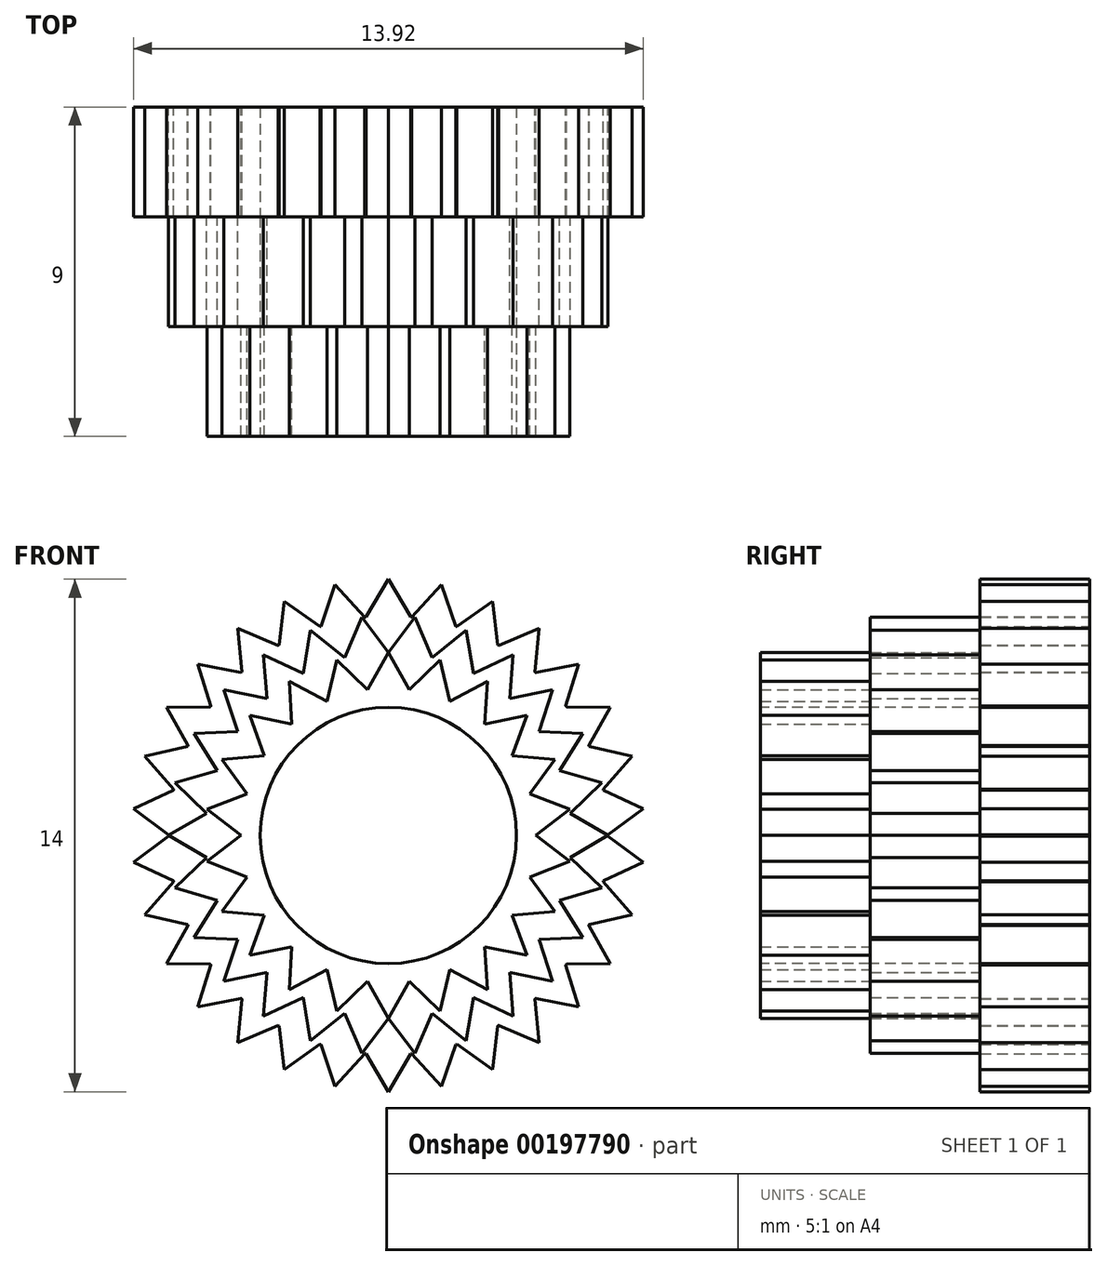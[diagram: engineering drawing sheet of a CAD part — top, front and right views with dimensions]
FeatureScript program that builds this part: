
annotation { "Feature Type Name" : "Feature", "Feature Type Description" : "" }
export const myFeature = defineFeature(function(context is Context, id is Id, definition is map)
    precondition{}
    {
        {
            var Q0;
            Q0=qCreatedBy(makeId("Front.planeOp"),FACE);
            var sketch = newSketch(context, id + "F0", { "sketchPlane" : qUnion([Q0])});
            skCircle(sketch, "E0", {"center": v(0, 0) * mm, "radius": 6 * mm});
            skLineSegment(sketch, "E1", {"start": v(0, 6) * mm, "end": v(0, 7) * mm, "construction": true});
            skLineSegment(sketch, "E2", {"start": v(0, 7) * mm, "end": v(-0.61, 5.97) * mm});
            skLineSegment(sketch, "E3.MirrorCS", {"start": v(0, 7) * mm, "end": v(0.61, 5.97) * mm});
            skLineSegment(sketch, "E4.1.0", {"start": v(-1.46, 6.85) * mm, "end": v(-0.64, 5.97) * mm});
            skLineSegment(sketch, "E4.1.1", {"start": v(-1.46, 6.85) * mm, "end": v(-1.84, 5.71) * mm});
            skLineSegment(sketch, "E4.2.0", {"start": v(-2.85, 6.4) * mm, "end": v(-1.87, 5.7) * mm});
            skLineSegment(sketch, "E4.2.1", {"start": v(-2.85, 6.4) * mm, "end": v(-2.99, 5.2) * mm});
            skLineSegment(sketch, "E4.3.0", {"start": v(-4.11, 5.66) * mm, "end": v(-3.01, 5.19) * mm});
            skLineSegment(sketch, "E4.3.1", {"start": v(-4.11, 5.66) * mm, "end": v(-4, 4.47) * mm});
            skLineSegment(sketch, "E4.4.0", {"start": v(-5.2, 4.68) * mm, "end": v(-4.03, 4.45) * mm});
            skLineSegment(sketch, "E4.4.1", {"start": v(-5.2, 4.68) * mm, "end": v(-4.85, 3.54) * mm});
            skLineSegment(sketch, "E4.5.0", {"start": v(-6.06, 3.5) * mm, "end": v(-4.86, 3.52) * mm});
            skLineSegment(sketch, "E4.5.1", {"start": v(-6.06, 3.5) * mm, "end": v(-5.48, 2.45) * mm});
            skLineSegment(sketch, "E4.6.0", {"start": v(-6.66, 2.16) * mm, "end": v(-5.49, 2.43) * mm});
            skLineSegment(sketch, "E4.6.1", {"start": v(-6.66, 2.16) * mm, "end": v(-5.87, 1.26) * mm});
            skLineSegment(sketch, "E4.7.0", {"start": v(-6.96, 0.73) * mm, "end": v(-5.87, 1.23) * mm});
            skLineSegment(sketch, "E4.7.1", {"start": v(-6.96, 0.73) * mm, "end": v(-6, 0.01) * mm});
            skLineSegment(sketch, "E4.8.0", {"start": v(-6.96, -0.73) * mm, "end": v(-6, -0.01) * mm});
            skLineSegment(sketch, "E4.8.1", {"start": v(-6.96, -0.73) * mm, "end": v(-5.87, -1.23) * mm});
            skLineSegment(sketch, "E4.9.0", {"start": v(-6.66, -2.16) * mm, "end": v(-5.87, -1.26) * mm});
            skLineSegment(sketch, "E4.9.1", {"start": v(-6.66, -2.16) * mm, "end": v(-5.49, -2.43) * mm});
            skLineSegment(sketch, "E4.10.0", {"start": v(-6.06, -3.5) * mm, "end": v(-5.48, -2.45) * mm});
            skLineSegment(sketch, "E4.10.1", {"start": v(-6.06, -3.5) * mm, "end": v(-4.86, -3.52) * mm});
            skLineSegment(sketch, "E4.11.0", {"start": v(-5.2, -4.68) * mm, "end": v(-4.85, -3.54) * mm});
            skLineSegment(sketch, "E4.11.1", {"start": v(-5.2, -4.68) * mm, "end": v(-4.03, -4.45) * mm});
            skLineSegment(sketch, "E4.12.0", {"start": v(-4.11, -5.66) * mm, "end": v(-4, -4.47) * mm});
            skLineSegment(sketch, "E4.12.1", {"start": v(-4.11, -5.66) * mm, "end": v(-3.01, -5.19) * mm});
            skLineSegment(sketch, "E4.13.0", {"start": v(-2.85, -6.4) * mm, "end": v(-2.99, -5.2) * mm});
            skLineSegment(sketch, "E4.13.1", {"start": v(-2.85, -6.4) * mm, "end": v(-1.87, -5.7) * mm});
            skLineSegment(sketch, "E4.14.0", {"start": v(-1.46, -6.85) * mm, "end": v(-1.84, -5.71) * mm});
            skLineSegment(sketch, "E4.14.1", {"start": v(-1.46, -6.85) * mm, "end": v(-0.64, -5.97) * mm});
            skLineSegment(sketch, "E4.15.0", {"start": v(0, -7) * mm, "end": v(-0.61, -5.97) * mm});
            skLineSegment(sketch, "E4.15.1", {"start": v(0, -7) * mm, "end": v(0.61, -5.97) * mm});
            skLineSegment(sketch, "E4.16.0", {"start": v(1.46, -6.85) * mm, "end": v(0.64, -5.97) * mm});
            skLineSegment(sketch, "E4.16.1", {"start": v(1.46, -6.85) * mm, "end": v(1.84, -5.71) * mm});
            skLineSegment(sketch, "E4.17.0", {"start": v(2.85, -6.4) * mm, "end": v(1.87, -5.7) * mm});
            skLineSegment(sketch, "E4.17.1", {"start": v(2.85, -6.4) * mm, "end": v(2.99, -5.2) * mm});
            skLineSegment(sketch, "E4.18.0", {"start": v(4.11, -5.66) * mm, "end": v(3.01, -5.19) * mm});
            skLineSegment(sketch, "E4.18.1", {"start": v(4.11, -5.66) * mm, "end": v(4, -4.47) * mm});
            skLineSegment(sketch, "E4.19.0", {"start": v(5.2, -4.68) * mm, "end": v(4.03, -4.45) * mm});
            skLineSegment(sketch, "E4.19.1", {"start": v(5.2, -4.68) * mm, "end": v(4.85, -3.54) * mm});
            skLineSegment(sketch, "E4.20.0", {"start": v(6.06, -3.5) * mm, "end": v(4.86, -3.52) * mm});
            skLineSegment(sketch, "E4.20.1", {"start": v(6.06, -3.5) * mm, "end": v(5.48, -2.45) * mm});
            skLineSegment(sketch, "E4.21.0", {"start": v(6.66, -2.16) * mm, "end": v(5.49, -2.43) * mm});
            skLineSegment(sketch, "E4.21.1", {"start": v(6.66, -2.16) * mm, "end": v(5.87, -1.26) * mm});
            skLineSegment(sketch, "E4.22.0", {"start": v(6.96, -0.73) * mm, "end": v(5.87, -1.23) * mm});
            skLineSegment(sketch, "E4.22.1", {"start": v(6.96, -0.73) * mm, "end": v(6, -0.01) * mm});
            skLineSegment(sketch, "E4.23.0", {"start": v(6.96, 0.73) * mm, "end": v(6, 0.01) * mm});
            skLineSegment(sketch, "E4.23.1", {"start": v(6.96, 0.73) * mm, "end": v(5.87, 1.23) * mm});
            skLineSegment(sketch, "E4.24.0", {"start": v(6.66, 2.16) * mm, "end": v(5.87, 1.26) * mm});
            skLineSegment(sketch, "E4.24.1", {"start": v(6.66, 2.16) * mm, "end": v(5.49, 2.43) * mm});
            skLineSegment(sketch, "E4.25.0", {"start": v(6.06, 3.5) * mm, "end": v(5.48, 2.45) * mm});
            skLineSegment(sketch, "E4.25.1", {"start": v(6.06, 3.5) * mm, "end": v(4.86, 3.52) * mm});
            skLineSegment(sketch, "E4.26.0", {"start": v(5.2, 4.68) * mm, "end": v(4.85, 3.54) * mm});
            skLineSegment(sketch, "E4.26.1", {"start": v(5.2, 4.68) * mm, "end": v(4.03, 4.45) * mm});
            skLineSegment(sketch, "E4.27.0", {"start": v(4.11, 5.66) * mm, "end": v(4, 4.47) * mm});
            skLineSegment(sketch, "E4.27.1", {"start": v(4.11, 5.66) * mm, "end": v(3.01, 5.19) * mm});
            skLineSegment(sketch, "E4.28.0", {"start": v(2.85, 6.4) * mm, "end": v(2.99, 5.2) * mm});
            skLineSegment(sketch, "E4.28.1", {"start": v(2.85, 6.4) * mm, "end": v(1.87, 5.7) * mm});
            skLineSegment(sketch, "E4.29.0", {"start": v(1.46, 6.85) * mm, "end": v(1.84, 5.71) * mm});
            skLineSegment(sketch, "E4.29.1", {"start": v(1.46, 6.85) * mm, "end": v(0.64, 5.97) * mm});
            skSolve(sketch);
        }
        {
            var Q0;
            Q0 = qSketchRegion(id + "F0", true);
            extrude(context, id + "F1", {"entities" : qUnion([Q0]), "depth" : 3 * mm});
        }
        {
            var Q0;
            Q0=makeQuery(id+"F1.opExtrude","CAP_FACE",FACE,{"disambiguationData":[OSD([sQuery(id+"F0.wireOp",EDGE,"E0"),sQuery(id+"F0.wireOp",EDGE,"E2"),sQuery(id+"F0.wireOp",EDGE,"E3.MirrorCS"),sQuery(id+"F0.wireOp",EDGE,"E4.1.0"),sQuery(id+"F0.wireOp",EDGE,"E4.1.1"),sQuery(id+"F0.wireOp",EDGE,"E4.2.0"),sQuery(id+"F0.wireOp",EDGE,"E4.2.1"),sQuery(id+"F0.wireOp",EDGE,"E4.3.0"),sQuery(id+"F0.wireOp",EDGE,"E4.3.1"),sQuery(id+"F0.wireOp",EDGE,"E4.4.0"),sQuery(id+"F0.wireOp",EDGE,"E4.4.1"),sQuery(id+"F0.wireOp",EDGE,"E4.5.0"),sQuery(id+"F0.wireOp",EDGE,"E4.5.1"),sQuery(id+"F0.wireOp",EDGE,"E4.6.0"),sQuery(id+"F0.wireOp",EDGE,"E4.6.1"),sQuery(id+"F0.wireOp",EDGE,"E4.7.0"),sQuery(id+"F0.wireOp",EDGE,"E4.7.1"),sQuery(id+"F0.wireOp",EDGE,"E4.8.0"),sQuery(id+"F0.wireOp",EDGE,"E4.8.1"),sQuery(id+"F0.wireOp",EDGE,"E4.9.0"),sQuery(id+"F0.wireOp",EDGE,"E4.9.1"),sQuery(id+"F0.wireOp",EDGE,"E4.10.0"),sQuery(id+"F0.wireOp",EDGE,"E4.10.1"),sQuery(id+"F0.wireOp",EDGE,"E4.11.0"),sQuery(id+"F0.wireOp",EDGE,"E4.11.1"),sQuery(id+"F0.wireOp",EDGE,"E4.12.0"),sQuery(id+"F0.wireOp",EDGE,"E4.12.1"),sQuery(id+"F0.wireOp",EDGE,"E4.13.0"),sQuery(id+"F0.wireOp",EDGE,"E4.13.1"),sQuery(id+"F0.wireOp",EDGE,"E4.14.0"),sQuery(id+"F0.wireOp",EDGE,"E4.14.1"),sQuery(id+"F0.wireOp",EDGE,"E4.15.0"),sQuery(id+"F0.wireOp",EDGE,"E4.15.1"),sQuery(id+"F0.wireOp",EDGE,"E4.16.0"),sQuery(id+"F0.wireOp",EDGE,"E4.16.1"),sQuery(id+"F0.wireOp",EDGE,"E4.17.0"),sQuery(id+"F0.wireOp",EDGE,"E4.17.1"),sQuery(id+"F0.wireOp",EDGE,"E4.18.0"),sQuery(id+"F0.wireOp",EDGE,"E4.18.1"),sQuery(id+"F0.wireOp",EDGE,"E4.19.0"),sQuery(id+"F0.wireOp",EDGE,"E4.19.1"),sQuery(id+"F0.wireOp",EDGE,"E4.20.0"),sQuery(id+"F0.wireOp",EDGE,"E4.20.1"),sQuery(id+"F0.wireOp",EDGE,"E4.21.0"),sQuery(id+"F0.wireOp",EDGE,"E4.21.1"),sQuery(id+"F0.wireOp",EDGE,"E4.22.0"),sQuery(id+"F0.wireOp",EDGE,"E4.22.1"),sQuery(id+"F0.wireOp",EDGE,"E4.23.0"),sQuery(id+"F0.wireOp",EDGE,"E4.23.1"),sQuery(id+"F0.wireOp",EDGE,"E4.24.0"),sQuery(id+"F0.wireOp",EDGE,"E4.24.1"),sQuery(id+"F0.wireOp",EDGE,"E4.25.0"),sQuery(id+"F0.wireOp",EDGE,"E4.25.1"),sQuery(id+"F0.wireOp",EDGE,"E4.26.0"),sQuery(id+"F0.wireOp",EDGE,"E4.26.1"),sQuery(id+"F0.wireOp",EDGE,"E4.27.0"),sQuery(id+"F0.wireOp",EDGE,"E4.27.1"),sQuery(id+"F0.wireOp",EDGE,"E4.28.0"),sQuery(id+"F0.wireOp",EDGE,"E4.28.1"),sQuery(id+"F0.wireOp",EDGE,"E4.29.0"),sQuery(id+"F0.wireOp",EDGE,"E4.29.1")])],"isStart":false});
            var sketch = newSketch(context, id + "F2", { "sketchPlane" : qUnion([Q0])});
            skCircle(sketch, "E5", {"center": v(0, 0) * mm, "radius": 5 * mm});
            skLineSegment(sketch, "E6", {"start": v(5, 0) * mm, "end": v(6, 0) * mm, "construction": true});
            skLineSegment(sketch, "E7", {"start": v(6, 0) * mm, "end": v(4.96, 0.6) * mm});
            skLineSegment(sketch, "E8.MirrorCS", {"start": v(6, 0) * mm, "end": v(4.96, -0.6) * mm});
            skLineSegment(sketch, "E9.1.0", {"start": v(5.83, 1.44) * mm, "end": v(4.67, 1.77) * mm});
            skLineSegment(sketch, "E9.1.1", {"start": v(5.83, 1.44) * mm, "end": v(4.96, 0.6) * mm});
            skLineSegment(sketch, "E9.2.0", {"start": v(5.31, 2.79) * mm, "end": v(4.11, 2.84) * mm});
            skLineSegment(sketch, "E9.2.1", {"start": v(5.31, 2.79) * mm, "end": v(4.68, 1.77) * mm});
            skLineSegment(sketch, "E9.3.0", {"start": v(4.5, 3.98) * mm, "end": v(3.31, 3.74) * mm});
            skLineSegment(sketch, "E9.3.1", {"start": v(4.5, 3.98) * mm, "end": v(4.12, 2.84) * mm});
            skLineSegment(sketch, "E9.4.0", {"start": v(3.4, 4.94) * mm, "end": v(2.32, 4.43) * mm});
            skLineSegment(sketch, "E9.4.1", {"start": v(3.4, 4.94) * mm, "end": v(3.32, 3.74) * mm});
            skLineSegment(sketch, "E9.5.0", {"start": v(2.13, 5.61) * mm, "end": v(1.2, 4.86) * mm});
            skLineSegment(sketch, "E9.5.1", {"start": v(2.13, 5.61) * mm, "end": v(2.33, 4.43) * mm});
            skLineSegment(sketch, "E9.6.0", {"start": v(0.72, 5.96) * mm, "end": v(0, 5) * mm});
            skLineSegment(sketch, "E9.6.1", {"start": v(0.72, 5.96) * mm, "end": v(1.2, 4.85) * mm});
            skLineSegment(sketch, "E9.7.0", {"start": v(-0.72, 5.96) * mm, "end": v(-1.2, 4.85) * mm});
            skLineSegment(sketch, "E9.7.1", {"start": v(-0.72, 5.96) * mm, "end": v(0, 5) * mm});
            skLineSegment(sketch, "E9.8.0", {"start": v(-2.13, 5.61) * mm, "end": v(-2.33, 4.43) * mm});
            skLineSegment(sketch, "E9.8.1", {"start": v(-2.13, 5.61) * mm, "end": v(-1.2, 4.86) * mm});
            skLineSegment(sketch, "E9.9.0", {"start": v(-3.4, 4.94) * mm, "end": v(-3.32, 3.74) * mm});
            skLineSegment(sketch, "E9.9.1", {"start": v(-3.4, 4.94) * mm, "end": v(-2.32, 4.43) * mm});
            skLineSegment(sketch, "E9.10.0", {"start": v(-4.5, 3.98) * mm, "end": v(-4.12, 2.84) * mm});
            skLineSegment(sketch, "E9.10.1", {"start": v(-4.5, 3.98) * mm, "end": v(-3.31, 3.74) * mm});
            skLineSegment(sketch, "E9.11.0", {"start": v(-5.31, 2.79) * mm, "end": v(-4.68, 1.77) * mm});
            skLineSegment(sketch, "E9.11.1", {"start": v(-5.31, 2.79) * mm, "end": v(-4.11, 2.84) * mm});
            skLineSegment(sketch, "E9.12.0", {"start": v(-5.83, 1.44) * mm, "end": v(-4.96, 0.6) * mm});
            skLineSegment(sketch, "E9.12.1", {"start": v(-5.83, 1.44) * mm, "end": v(-4.67, 1.77) * mm});
            skLineSegment(sketch, "E9.13.0", {"start": v(-6, 0) * mm, "end": v(-4.96, -0.6) * mm});
            skLineSegment(sketch, "E9.13.1", {"start": v(-6, 0) * mm, "end": v(-4.96, 0.6) * mm});
            skLineSegment(sketch, "E9.14.0", {"start": v(-5.83, -1.44) * mm, "end": v(-4.67, -1.77) * mm});
            skLineSegment(sketch, "E9.14.1", {"start": v(-5.83, -1.44) * mm, "end": v(-4.96, -0.6) * mm});
            skLineSegment(sketch, "E9.15.0", {"start": v(-5.31, -2.79) * mm, "end": v(-4.11, -2.84) * mm});
            skLineSegment(sketch, "E9.15.1", {"start": v(-5.31, -2.79) * mm, "end": v(-4.68, -1.77) * mm});
            skLineSegment(sketch, "E9.16.0", {"start": v(-4.5, -3.98) * mm, "end": v(-3.31, -3.74) * mm});
            skLineSegment(sketch, "E9.16.1", {"start": v(-4.5, -3.98) * mm, "end": v(-4.12, -2.84) * mm});
            skLineSegment(sketch, "E9.17.0", {"start": v(-3.4, -4.94) * mm, "end": v(-2.32, -4.43) * mm});
            skLineSegment(sketch, "E9.17.1", {"start": v(-3.4, -4.94) * mm, "end": v(-3.32, -3.74) * mm});
            skLineSegment(sketch, "E9.18.0", {"start": v(-2.13, -5.61) * mm, "end": v(-1.2, -4.86) * mm});
            skLineSegment(sketch, "E9.18.1", {"start": v(-2.13, -5.61) * mm, "end": v(-2.33, -4.43) * mm});
            skLineSegment(sketch, "E9.19.0", {"start": v(-0.72, -5.96) * mm, "end": v(0, -5) * mm});
            skLineSegment(sketch, "E9.19.1", {"start": v(-0.72, -5.96) * mm, "end": v(-1.2, -4.85) * mm});
            skLineSegment(sketch, "E9.20.0", {"start": v(0.72, -5.96) * mm, "end": v(1.2, -4.85) * mm});
            skLineSegment(sketch, "E9.20.1", {"start": v(0.72, -5.96) * mm, "end": v(0, -5) * mm});
            skLineSegment(sketch, "E9.21.0", {"start": v(2.13, -5.61) * mm, "end": v(2.33, -4.43) * mm});
            skLineSegment(sketch, "E9.21.1", {"start": v(2.13, -5.61) * mm, "end": v(1.2, -4.86) * mm});
            skLineSegment(sketch, "E9.22.0", {"start": v(3.4, -4.94) * mm, "end": v(3.32, -3.74) * mm});
            skLineSegment(sketch, "E9.22.1", {"start": v(3.4, -4.94) * mm, "end": v(2.32, -4.43) * mm});
            skLineSegment(sketch, "E9.23.0", {"start": v(4.5, -3.98) * mm, "end": v(4.12, -2.84) * mm});
            skLineSegment(sketch, "E9.23.1", {"start": v(4.5, -3.98) * mm, "end": v(3.31, -3.74) * mm});
            skLineSegment(sketch, "E9.24.0", {"start": v(5.31, -2.79) * mm, "end": v(4.68, -1.77) * mm});
            skLineSegment(sketch, "E9.24.1", {"start": v(5.31, -2.79) * mm, "end": v(4.11, -2.84) * mm});
            skLineSegment(sketch, "E9.25.0", {"start": v(5.83, -1.44) * mm, "end": v(4.96, -0.6) * mm});
            skLineSegment(sketch, "E9.25.1", {"start": v(5.83, -1.44) * mm, "end": v(4.67, -1.77) * mm});
            skSolve(sketch);
        }
        {
            var Q0;
            Q0 = qSketchRegion(id + "F2", true);
            var Q1;
            {var subQ0=sQuery(id+"F2.wireOp",EDGE,"E5");var subQ42=makeQuery(id+"F2.imprint","INTERSECT",VERTEX,{"derivedFrom":[subQ0,sQuery(id+"F2.wireOp",EDGE,"E7")]});Q1=makeQuery(id+"F2.imprint","IMPRINT",FACE,{"disambiguationData":[TD([[makeQuery(id+"F2.imprint","IMPRINT",EDGE,{"disambiguationData":[TD([[subQ42,1.0]])],"derivedFrom":subQ0}),1.0]])]});}
            extrude(context, id + "F3", {"entities" : qUnion([Q0, Q1]), "depth" : 3 * mm});
        }
        {
            var Q0;
            Q0=makeQuery(id+"F3.opExtrude","CAP_FACE",FACE,{"disambiguationData":[OSD([sQuery(id+"F2.wireOp",EDGE,"E7"),sQuery(id+"F2.wireOp",EDGE,"E8.MirrorCS"),sQuery(id+"F2.wireOp",EDGE,"E9.1.0"),sQuery(id+"F2.wireOp",EDGE,"E9.1.1"),sQuery(id+"F2.wireOp",EDGE,"E9.2.0"),sQuery(id+"F2.wireOp",EDGE,"E9.2.1"),sQuery(id+"F2.wireOp",EDGE,"E9.3.0"),sQuery(id+"F2.wireOp",EDGE,"E9.3.1"),sQuery(id+"F2.wireOp",EDGE,"E9.4.0"),sQuery(id+"F2.wireOp",EDGE,"E9.4.1"),sQuery(id+"F2.wireOp",EDGE,"E9.5.0"),sQuery(id+"F2.wireOp",EDGE,"E9.5.1"),sQuery(id+"F2.wireOp",EDGE,"E9.6.0"),sQuery(id+"F2.wireOp",EDGE,"E9.6.1"),sQuery(id+"F2.wireOp",EDGE,"E9.7.0"),sQuery(id+"F2.wireOp",EDGE,"E9.7.1"),sQuery(id+"F2.wireOp",EDGE,"E9.8.0"),sQuery(id+"F2.wireOp",EDGE,"E9.8.1"),sQuery(id+"F2.wireOp",EDGE,"E9.9.0"),sQuery(id+"F2.wireOp",EDGE,"E9.9.1"),sQuery(id+"F2.wireOp",EDGE,"E9.10.0"),sQuery(id+"F2.wireOp",EDGE,"E9.10.1"),sQuery(id+"F2.wireOp",EDGE,"E9.11.0"),sQuery(id+"F2.wireOp",EDGE,"E9.11.1"),sQuery(id+"F2.wireOp",EDGE,"E9.12.0"),sQuery(id+"F2.wireOp",EDGE,"E9.12.1"),sQuery(id+"F2.wireOp",EDGE,"E9.13.0"),sQuery(id+"F2.wireOp",EDGE,"E9.13.1"),sQuery(id+"F2.wireOp",EDGE,"E9.14.0"),sQuery(id+"F2.wireOp",EDGE,"E9.14.1"),sQuery(id+"F2.wireOp",EDGE,"E9.15.0"),sQuery(id+"F2.wireOp",EDGE,"E9.15.1"),sQuery(id+"F2.wireOp",EDGE,"E9.16.0"),sQuery(id+"F2.wireOp",EDGE,"E9.16.1"),sQuery(id+"F2.wireOp",EDGE,"E9.17.0"),sQuery(id+"F2.wireOp",EDGE,"E9.17.1"),sQuery(id+"F2.wireOp",EDGE,"E9.18.0"),sQuery(id+"F2.wireOp",EDGE,"E9.18.1"),sQuery(id+"F2.wireOp",EDGE,"E9.19.0"),sQuery(id+"F2.wireOp",EDGE,"E9.19.1"),sQuery(id+"F2.wireOp",EDGE,"E9.20.0"),sQuery(id+"F2.wireOp",EDGE,"E9.20.1"),sQuery(id+"F2.wireOp",EDGE,"E9.21.0"),sQuery(id+"F2.wireOp",EDGE,"E9.21.1"),sQuery(id+"F2.wireOp",EDGE,"E9.22.0"),sQuery(id+"F2.wireOp",EDGE,"E9.22.1"),sQuery(id+"F2.wireOp",EDGE,"E9.23.0"),sQuery(id+"F2.wireOp",EDGE,"E9.23.1"),sQuery(id+"F2.wireOp",EDGE,"E9.24.0"),sQuery(id+"F2.wireOp",EDGE,"E9.24.1"),sQuery(id+"F2.wireOp",EDGE,"E9.25.0"),sQuery(id+"F2.wireOp",EDGE,"E9.25.1")])],"isStart":false});
            var sketch = newSketch(context, id + "F4", { "sketchPlane" : qUnion([Q0])});
            skCircle(sketch, "E10", {"center": v(0, 0) * mm, "radius": 4 * mm});
            skLineSegment(sketch, "E11", {"start": v(0, 4) * mm, "end": v(0, 5) * mm, "construction": true});
            skLineSegment(sketch, "E12", {"start": v(0, 5) * mm, "end": v(-0.59, 3.96) * mm});
            skLineSegment(sketch, "E13.MirrorCS", {"start": v(0, 5) * mm, "end": v(0.59, 3.96) * mm});
            skLineSegment(sketch, "E14.1.0", {"start": v(-1.4, 4.8) * mm, "end": v(-1.68, 3.63) * mm});
            skLineSegment(sketch, "E14.1.1", {"start": v(-1.4, 4.8) * mm, "end": v(-0.55, 3.96) * mm});
            skLineSegment(sketch, "E14.2.0", {"start": v(-2.7, 4.2) * mm, "end": v(-2.63, 3.01) * mm});
            skLineSegment(sketch, "E14.2.1", {"start": v(-2.7, 4.2) * mm, "end": v(-1.64, 3.65) * mm});
            skLineSegment(sketch, "E14.3.0", {"start": v(-3.78, 3.28) * mm, "end": v(-3.38, 2.15) * mm});
            skLineSegment(sketch, "E14.3.1", {"start": v(-3.78, 3.28) * mm, "end": v(-2.6, 3.04) * mm});
            skLineSegment(sketch, "E14.4.0", {"start": v(-4.55, 2.08) * mm, "end": v(-3.84, 1.1) * mm});
            skLineSegment(sketch, "E14.4.1", {"start": v(-4.55, 2.08) * mm, "end": v(-3.35, 2.18) * mm});
            skLineSegment(sketch, "E14.5.0", {"start": v(-4.95, 0.71) * mm, "end": v(-4, -0.02) * mm});
            skLineSegment(sketch, "E14.5.1", {"start": v(-4.95, 0.71) * mm, "end": v(-3.83, 1.15) * mm});
            skLineSegment(sketch, "E14.6.0", {"start": v(-4.95, -0.71) * mm, "end": v(-3.83, -1.15) * mm});
            skLineSegment(sketch, "E14.6.1", {"start": v(-4.95, -0.71) * mm, "end": v(-4, 0.02) * mm});
            skLineSegment(sketch, "E14.7.0", {"start": v(-4.55, -2.08) * mm, "end": v(-3.35, -2.18) * mm});
            skLineSegment(sketch, "E14.7.1", {"start": v(-4.55, -2.08) * mm, "end": v(-3.84, -1.1) * mm});
            skLineSegment(sketch, "E14.8.0", {"start": v(-3.78, -3.28) * mm, "end": v(-2.6, -3.04) * mm});
            skLineSegment(sketch, "E14.8.1", {"start": v(-3.78, -3.28) * mm, "end": v(-3.38, -2.15) * mm});
            skLineSegment(sketch, "E14.9.0", {"start": v(-2.7, -4.2) * mm, "end": v(-1.64, -3.65) * mm});
            skLineSegment(sketch, "E14.9.1", {"start": v(-2.7, -4.2) * mm, "end": v(-2.63, -3.01) * mm});
            skLineSegment(sketch, "E14.10.0", {"start": v(-1.4, -4.8) * mm, "end": v(-0.55, -3.96) * mm});
            skLineSegment(sketch, "E14.10.1", {"start": v(-1.4, -4.8) * mm, "end": v(-1.68, -3.63) * mm});
            skLineSegment(sketch, "E14.11.0", {"start": v(0, -5) * mm, "end": v(0.59, -3.96) * mm});
            skLineSegment(sketch, "E14.11.1", {"start": v(0, -5) * mm, "end": v(-0.59, -3.96) * mm});
            skLineSegment(sketch, "E14.12.0", {"start": v(1.4, -4.8) * mm, "end": v(1.68, -3.63) * mm});
            skLineSegment(sketch, "E14.12.1", {"start": v(1.4, -4.8) * mm, "end": v(0.55, -3.96) * mm});
            skLineSegment(sketch, "E14.13.0", {"start": v(2.7, -4.2) * mm, "end": v(2.63, -3.01) * mm});
            skLineSegment(sketch, "E14.13.1", {"start": v(2.7, -4.2) * mm, "end": v(1.64, -3.65) * mm});
            skLineSegment(sketch, "E14.14.0", {"start": v(3.78, -3.28) * mm, "end": v(3.38, -2.15) * mm});
            skLineSegment(sketch, "E14.14.1", {"start": v(3.78, -3.28) * mm, "end": v(2.6, -3.04) * mm});
            skLineSegment(sketch, "E14.15.0", {"start": v(4.55, -2.08) * mm, "end": v(3.84, -1.1) * mm});
            skLineSegment(sketch, "E14.15.1", {"start": v(4.55, -2.08) * mm, "end": v(3.35, -2.18) * mm});
            skLineSegment(sketch, "E14.16.0", {"start": v(4.95, -0.71) * mm, "end": v(4, 0.02) * mm});
            skLineSegment(sketch, "E14.16.1", {"start": v(4.95, -0.71) * mm, "end": v(3.83, -1.15) * mm});
            skLineSegment(sketch, "E14.17.0", {"start": v(4.95, 0.71) * mm, "end": v(3.83, 1.15) * mm});
            skLineSegment(sketch, "E14.17.1", {"start": v(4.95, 0.71) * mm, "end": v(4, -0.02) * mm});
            skLineSegment(sketch, "E14.18.0", {"start": v(4.55, 2.08) * mm, "end": v(3.35, 2.18) * mm});
            skLineSegment(sketch, "E14.18.1", {"start": v(4.55, 2.08) * mm, "end": v(3.84, 1.1) * mm});
            skLineSegment(sketch, "E14.19.0", {"start": v(3.78, 3.28) * mm, "end": v(2.6, 3.04) * mm});
            skLineSegment(sketch, "E14.19.1", {"start": v(3.78, 3.28) * mm, "end": v(3.38, 2.15) * mm});
            skLineSegment(sketch, "E14.20.0", {"start": v(2.7, 4.2) * mm, "end": v(1.64, 3.65) * mm});
            skLineSegment(sketch, "E14.20.1", {"start": v(2.7, 4.2) * mm, "end": v(2.63, 3.01) * mm});
            skLineSegment(sketch, "E14.21.0", {"start": v(1.4, 4.8) * mm, "end": v(0.55, 3.96) * mm});
            skLineSegment(sketch, "E14.21.1", {"start": v(1.4, 4.8) * mm, "end": v(1.68, 3.63) * mm});
            skSolve(sketch);
        }
        {
            var Q0;
            Q0 = qSketchRegion(id + "F4", true);
            var Q1;
            {var subQ0=sQuery(id+"F4.wireOp",EDGE,"E10");var subQ27=makeQuery(id+"F4.imprint","INTERSECT",VERTEX,{"derivedFrom":[subQ0,sQuery(id+"F4.wireOp",EDGE,"E14.16.0")]});Q1=makeQuery(id+"F4.imprint","IMPRINT",FACE,{"disambiguationData":[TD([[makeQuery(id+"F4.imprint","IMPRINT",EDGE,{"disambiguationData":[TD([[subQ27,-1.0]])],"derivedFrom":subQ0}),1.0]])]});}
            extrude(context, id + "F5", {"entities" : qUnion([Q0, Q1]), "depth" : 3 * mm});
        }
        {
            var Q0;
            Q0=makeQuery(id+"F5.opExtrude","CAP_FACE",FACE,{"disambiguationData":[OSD([sQuery(id+"F4.wireOp",EDGE,"E12"),sQuery(id+"F4.wireOp",EDGE,"E13.MirrorCS"),sQuery(id+"F4.wireOp",EDGE,"E14.1.0"),sQuery(id+"F4.wireOp",EDGE,"E14.1.1"),sQuery(id+"F4.wireOp",EDGE,"E14.2.0"),sQuery(id+"F4.wireOp",EDGE,"E14.2.1"),sQuery(id+"F4.wireOp",EDGE,"E14.3.0"),sQuery(id+"F4.wireOp",EDGE,"E14.3.1"),sQuery(id+"F4.wireOp",EDGE,"E14.4.0"),sQuery(id+"F4.wireOp",EDGE,"E14.4.1"),sQuery(id+"F4.wireOp",EDGE,"E14.5.0"),sQuery(id+"F4.wireOp",EDGE,"E14.5.1"),sQuery(id+"F4.wireOp",EDGE,"E14.6.0"),sQuery(id+"F4.wireOp",EDGE,"E14.6.1"),sQuery(id+"F4.wireOp",EDGE,"E14.7.0"),sQuery(id+"F4.wireOp",EDGE,"E14.7.1"),sQuery(id+"F4.wireOp",EDGE,"E14.8.0"),sQuery(id+"F4.wireOp",EDGE,"E14.8.1"),sQuery(id+"F4.wireOp",EDGE,"E14.9.0"),sQuery(id+"F4.wireOp",EDGE,"E14.9.1"),sQuery(id+"F4.wireOp",EDGE,"E14.10.0"),sQuery(id+"F4.wireOp",EDGE,"E14.10.1"),sQuery(id+"F4.wireOp",EDGE,"E14.11.0"),sQuery(id+"F4.wireOp",EDGE,"E14.11.1"),sQuery(id+"F4.wireOp",EDGE,"E14.12.0"),sQuery(id+"F4.wireOp",EDGE,"E14.12.1"),sQuery(id+"F4.wireOp",EDGE,"E14.13.0"),sQuery(id+"F4.wireOp",EDGE,"E14.13.1"),sQuery(id+"F4.wireOp",EDGE,"E14.14.0"),sQuery(id+"F4.wireOp",EDGE,"E14.14.1"),sQuery(id+"F4.wireOp",EDGE,"E14.15.0"),sQuery(id+"F4.wireOp",EDGE,"E14.15.1"),sQuery(id+"F4.wireOp",EDGE,"E14.16.0"),sQuery(id+"F4.wireOp",EDGE,"E14.16.1"),sQuery(id+"F4.wireOp",EDGE,"E14.17.0"),sQuery(id+"F4.wireOp",EDGE,"E14.17.1"),sQuery(id+"F4.wireOp",EDGE,"E14.18.0"),sQuery(id+"F4.wireOp",EDGE,"E14.18.1"),sQuery(id+"F4.wireOp",EDGE,"E14.19.0"),sQuery(id+"F4.wireOp",EDGE,"E14.19.1"),sQuery(id+"F4.wireOp",EDGE,"E14.20.0"),sQuery(id+"F4.wireOp",EDGE,"E14.20.1"),sQuery(id+"F4.wireOp",EDGE,"E14.21.0"),sQuery(id+"F4.wireOp",EDGE,"E14.21.1")])],"isStart":false});
            var sketch = newSketch(context, id + "F6", { "sketchPlane" : qUnion([Q0])});
            skCircle(sketch, "E15", {"center": v(0, 0) * mm, "radius": 3.5 * mm});
            skSolve(sketch);
        }
        {
            var Q0;
            Q0 = qSketchRegion(id + "F6", true);
            extrude(context, id + "F7", {"entities" : qUnion([Q0]), "operationType" : NewBodyOperationType.REMOVE, "oppositeDirection" : true, "depth" : 25 * mm});
        }
    });
